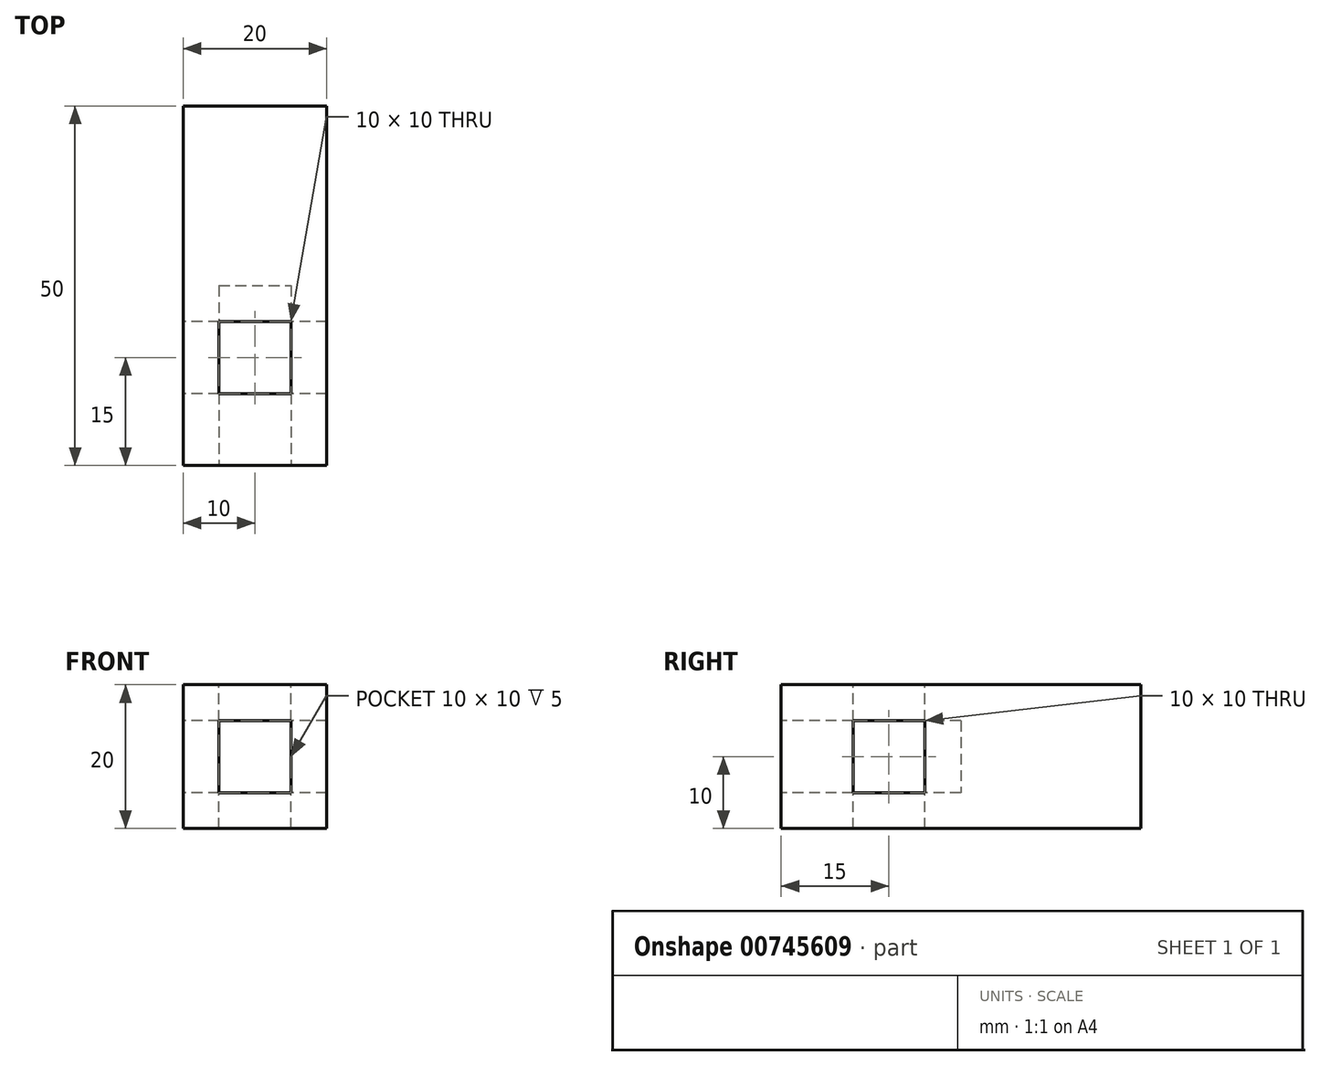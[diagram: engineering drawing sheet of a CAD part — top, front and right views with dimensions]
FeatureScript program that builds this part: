
annotation { "Feature Type Name" : "Feature", "Feature Type Description" : "" }
export const myFeature = defineFeature(function(context is Context, id is Id, definition is map)
    precondition{}
    {
        {
            var Q0;
            Q0=qCreatedBy(makeId("Front.planeOp"),FACE);
            var sketch = newSketch(context, id + "F0", { "sketchPlane" : qUnion([Q0])});
            skLineSegment(sketch, "E0.bottom", {"start": v(0, 0) * mm, "end": v(-20, 0) * mm});
            skLineSegment(sketch, "E0.top", {"start": v(0, 20) * mm, "end": v(-20, 20) * mm});
            skLineSegment(sketch, "E0.left", {"start": v(0, 0) * mm, "end": v(0, 20) * mm});
            skLineSegment(sketch, "E0.right", {"start": v(-20, 0) * mm, "end": v(-20, 20) * mm});
            skSolve(sketch);
        }
        {
            var Q0;
            Q0 = qSketchRegion(id + "F0", true);
            extrude(context, id + "F1", {"entities" : qUnion([Q0]), "depth" : 50 * mm, "offsetDistance" : 25 * mm});
        }
        {
            var Q0;
            Q0=makeQuery(id+"F1.opExtrude","CAP_FACE",FACE,{"disambiguationData":[OSD([sQuery(id+"F0.wireOp",EDGE,"E0.bottom"),sQuery(id+"F0.wireOp",EDGE,"E0.top"),sQuery(id+"F0.wireOp",EDGE,"E0.left"),sQuery(id+"F0.wireOp",EDGE,"E0.right")])],"isStart":false});
            var sketch = newSketch(context, id + "F2", { "sketchPlane" : qUnion([Q0])});
            skPoint(sketch, "E1", {"position": v(-10, 10) * mm});
            skLineSegment(sketch, "E2.bottom", {"start": v(-15, 15) * mm, "end": v(-5, 15) * mm});
            skLineSegment(sketch, "E2.top", {"start": v(-15, 5) * mm, "end": v(-5, 5) * mm});
            skLineSegment(sketch, "E2.left", {"start": v(-15, 15) * mm, "end": v(-15, 5) * mm});
            skLineSegment(sketch, "E2.right", {"start": v(-5, 15) * mm, "end": v(-5, 5) * mm});
            skSolve(sketch);
        }
        {
            var Q0;
            Q0 = qSketchRegion(id + "F2", true);
            extrude(context, id + "F3", {"entities" : qUnion([Q0]), "operationType" : NewBodyOperationType.REMOVE, "oppositeDirection" : true, "depth" : 25 * mm, "offsetDistance" : 25 * mm});
        }
        {
            var Q0;
            Q0=makeQuery(id+"F1.opExtrude","SWEPT_FACE",FACE,{"disambiguationData":[OSD([sQuery(id+"F0.wireOp",EDGE,"E0.top")])]});
            var sketch = newSketch(context, id + "F4", { "sketchPlane" : qUnion([Q0])});
            skPoint(sketch, "E3", {"position": v(-10, -35) * mm});
            skLineSegment(sketch, "E4.bottom", {"start": v(-15, -30) * mm, "end": v(-5, -30) * mm});
            skLineSegment(sketch, "E4.top", {"start": v(-15, -40) * mm, "end": v(-5, -40) * mm});
            skLineSegment(sketch, "E4.left", {"start": v(-15, -30) * mm, "end": v(-15, -40) * mm});
            skLineSegment(sketch, "E4.right", {"start": v(-5, -30) * mm, "end": v(-5, -40) * mm});
            skSolve(sketch);
        }
        {
            var Q0;
            Q0 = qSketchRegion(id + "F4", true);
            extrude(context, id + "F5", {"entities" : qUnion([Q0]), "operationType" : NewBodyOperationType.REMOVE, "oppositeDirection" : true, "depth" : 25 * mm, "offsetDistance" : 25 * mm});
        }
        {
            var Q0;
            Q0=makeQuery(id+"F1.opExtrude","SWEPT_FACE",FACE,{"disambiguationData":[OSD([sQuery(id+"F0.wireOp",EDGE,"E0.right")])]});
            var sketch = newSketch(context, id + "F6", { "sketchPlane" : qUnion([Q0])});
            skPoint(sketch, "E5", {"position": v(35, 10) * mm});
            skLineSegment(sketch, "E6.bottom", {"start": v(30, 15) * mm, "end": v(40, 15) * mm});
            skLineSegment(sketch, "E6.top", {"start": v(30, 5) * mm, "end": v(40, 5) * mm});
            skLineSegment(sketch, "E6.left", {"start": v(30, 15) * mm, "end": v(30, 5) * mm});
            skLineSegment(sketch, "E6.right", {"start": v(40, 15) * mm, "end": v(40, 5) * mm});
            skSolve(sketch);
        }
        {
            var Q0;
            Q0 = qSketchRegion(id + "F6", true);
            extrude(context, id + "F7", {"entities" : qUnion([Q0]), "operationType" : NewBodyOperationType.REMOVE, "oppositeDirection" : true, "depth" : 25 * mm, "offsetDistance" : 25 * mm});
        }
    });
